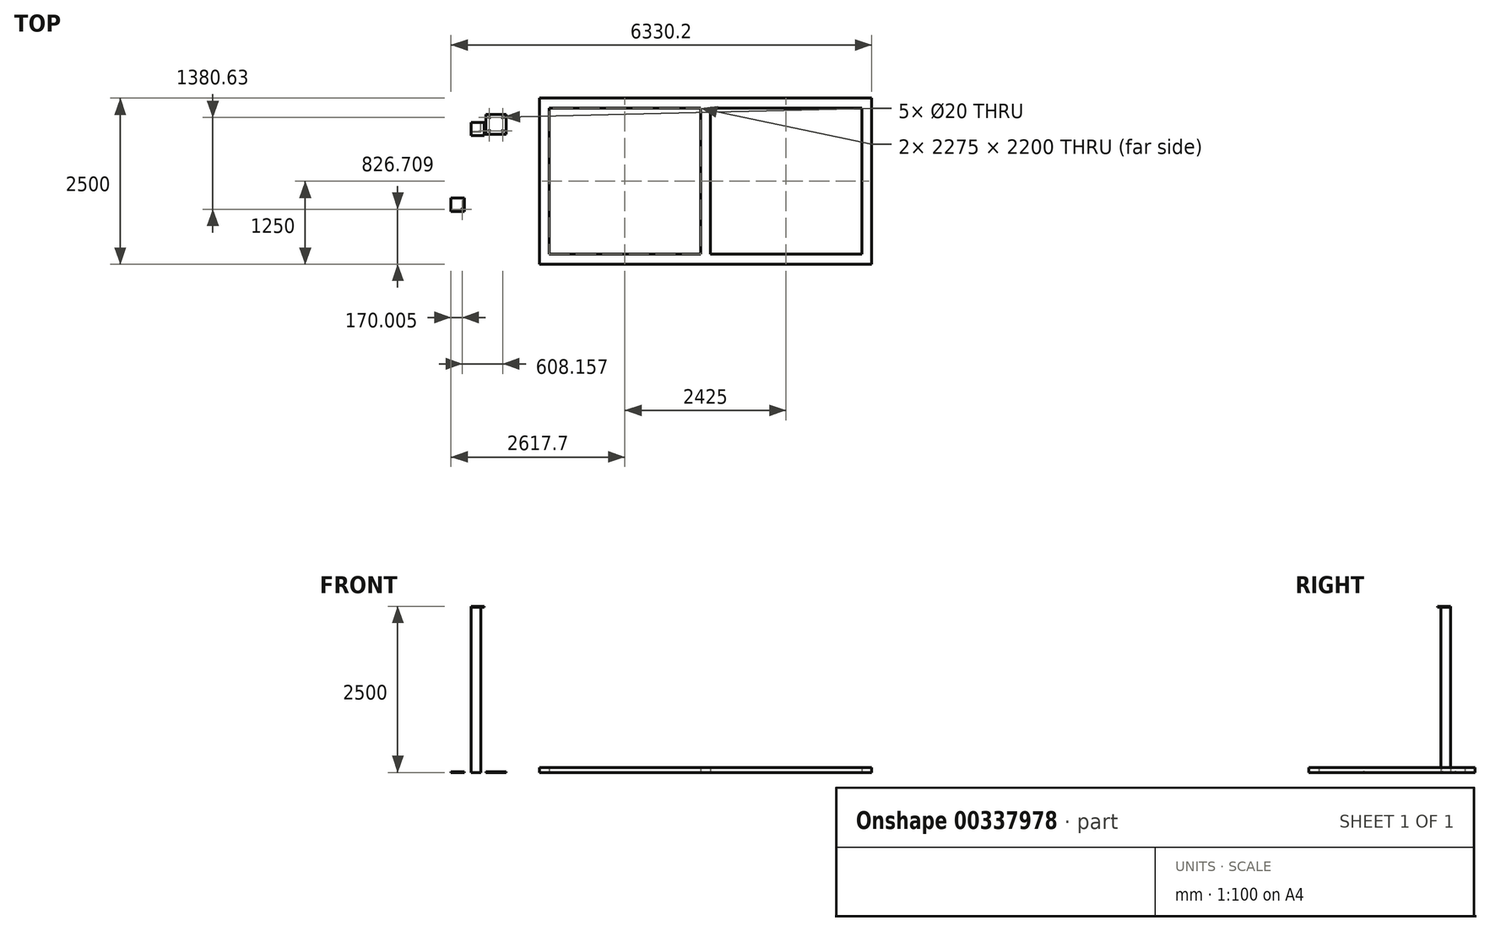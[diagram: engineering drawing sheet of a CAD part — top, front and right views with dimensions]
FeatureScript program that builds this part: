
annotation { "Feature Type Name" : "Feature", "Feature Type Description" : "" }
export const myFeature = defineFeature(function(context is Context, id is Id, definition is map)
    precondition{}
    {
        {
            var Q0;
            Q0=qCreatedBy(makeId("Top.planeOp"),FACE);
            var sketch = newSketch(context, id + "F0", { "sketchPlane" : qUnion([Q0])});
            skLineSegment(sketch, "E0.bottom", {"start": v(75, -75) * mm, "end": v(-75, -75) * mm});
            skLineSegment(sketch, "E0.top", {"start": v(75, 75) * mm, "end": v(-75, 75) * mm});
            skLineSegment(sketch, "E0.left", {"start": v(75, -75) * mm, "end": v(75, 75) * mm});
            skLineSegment(sketch, "E0.right", {"start": v(-75, -75) * mm, "end": v(-75, 75) * mm});
            skPoint(sketch, "E0.middle", {"position": v(0, 0) * mm});
            skLineSegment(sketch, "E1.0", {"start": v(70, 70) * mm, "end": v(-70, 70) * mm});
            skLineSegment(sketch, "E1.1", {"start": v(70, -70) * mm, "end": v(70, 70) * mm});
            skLineSegment(sketch, "E1.2", {"start": v(70, -70) * mm, "end": v(-70, -70) * mm});
            skLineSegment(sketch, "E1.3", {"start": v(-70, -70) * mm, "end": v(-70, 70) * mm});
            skLineSegment(sketch, "E2.bottom", {"start": v(451.01, -103.82) * mm, "end": v(151.01, -103.82) * mm});
            skLineSegment(sketch, "E2.top", {"start": v(451.01, 196.18) * mm, "end": v(151.01, 196.18) * mm});
            skLineSegment(sketch, "E2.left", {"start": v(451.01, -103.82) * mm, "end": v(451.01, 196.18) * mm});
            skLineSegment(sketch, "E2.right", {"start": v(151.01, -103.82) * mm, "end": v(151.01, 196.18) * mm});
            skCircle(sketch, "E3", {"center": v(401.01, 146.18) * mm, "radius": 10 * mm});
            skPoint(sketch, "E4", {"position": v(301.01, 46.18) * mm});
            skCircle(sketch, "E5.1.0", {"center": v(201.01, 146.18) * mm, "radius": 10 * mm});
            skCircle(sketch, "E5.2.0", {"center": v(201.01, -53.82) * mm, "radius": 10 * mm});
            skCircle(sketch, "E5.3.0", {"center": v(401.01, -53.82) * mm, "radius": 10 * mm});
            skLineSegment(sketch, "E6", {"start": v(953.05, 438.84) * mm, "end": v(953.05, -2061.16) * mm});
            skLineSegment(sketch, "E7", {"start": v(953.05, -2061.16) * mm, "end": v(5953.05, -2061.16) * mm});
            skLineSegment(sketch, "E8", {"start": v(5953.05, -2061.16) * mm, "end": v(5953.05, 438.84) * mm});
            skLineSegment(sketch, "E9.0", {"start": v(5803.05, -1911.16) * mm, "end": v(5803.05, 288.84) * mm});
            skLineSegment(sketch, "E9.1", {"start": v(1103.05, -1911.16) * mm, "end": v(3378.05, -1911.16) * mm});
            skLineSegment(sketch, "E9.2", {"start": v(1103.05, 288.84) * mm, "end": v(1103.05, -1911.16) * mm});
            skLineSegment(sketch, "E10.0", {"start": v(3528.05, 288.84) * mm, "end": v(3528.05, -1911.16) * mm});
            skLineSegment(sketch, "E11.0", {"start": v(3378.05, 288.84) * mm, "end": v(3378.05, -1911.16) * mm});
            skLineSegment(sketch, "E12.trimOffspring", {"start": v(3528.05, -1911.16) * mm, "end": v(5803.05, -1911.16) * mm});
            skLineSegment(sketch, "E13", {"start": v(953.05, 438.84) * mm, "end": v(1103.05, 438.84) * mm});
            skLineSegment(sketch, "E14", {"start": v(3378.05, 438.84) * mm, "end": v(3528.05, 438.84) * mm});
            skLineSegment(sketch, "E15", {"start": v(5803.05, 438.84) * mm, "end": v(5953.05, 438.84) * mm});
            skLineSegment(sketch, "E16", {"start": v(953.05, 438.84) * mm, "end": v(5953.05, 438.84) * mm});
            skLineSegment(sketch, "E17.0", {"start": v(1103.05, 288.84) * mm, "end": v(3378.05, 288.84) * mm});
            skLineSegment(sketch, "E18.trimOffspring", {"start": v(3528.05, 288.84) * mm, "end": v(5803.05, 288.84) * mm});
            skLineSegment(sketch, "E19.bottom", {"start": v(-177.15, -1264.45) * mm, "end": v(-377.15, -1264.45) * mm});
            skLineSegment(sketch, "E19.top", {"start": v(-177.15, -1064.45) * mm, "end": v(-377.15, -1064.45) * mm});
            skLineSegment(sketch, "E19.left", {"start": v(-177.15, -1264.45) * mm, "end": v(-177.15, -1064.45) * mm});
            skLineSegment(sketch, "E19.right", {"start": v(-377.15, -1264.45) * mm, "end": v(-377.15, -1064.45) * mm});
            skPoint(sketch, "E19.middle", {"position": v(-277.15, -1164.45) * mm});
            skCircle(sketch, "E20", {"center": v(-207.15, -1234.45) * mm, "radius": 10 * mm});
            skSolve(sketch);
        }
        {
            var Q0;
            Q0=makeQuery(id+"F0.imprint","IMPRINT",FACE,{"disambiguationData":[TD([[makeQuery(id+"F0.imprint","IMPRINT",EDGE,{"derivedFrom":sQuery(id+"F0.wireOp",EDGE,"E0.bottom")}),-1.0]])]});
            extrude(context, id + "F1", {"entities" : qUnion([Q0]), "depth" : 2500 * mm});
        }
        {
            var Q0;
            Q0=makeQuery(id+"F0.imprint","IMPRINT",FACE,{"disambiguationData":[TD([[makeQuery(id+"F0.imprint","IMPRINT",EDGE,{"derivedFrom":sQuery(id+"F0.wireOp",EDGE,"E2.bottom")}),-1.0]])]});
            extrude(context, id + "F2", {"entities" : qUnion([Q0]), "depth" : 10 * mm});
        }
        {
            var Q0;
            Q0=makeQuery(id+"F0.imprint","IMPRINT",FACE,{"disambiguationData":[TD([[makeQuery(id+"F0.imprint","IMPRINT",EDGE,{"derivedFrom":sQuery(id+"F0.wireOp",EDGE,"E6")}),1.0]])]});
            extrude(context, id + "F3", {"entities" : qUnion([Q0]), "depth" : 75 * mm});
        }
        {
            var Q0;
            Q0=makeQuery(id+"F0.imprint","IMPRINT",FACE,{"disambiguationData":[TD([[makeQuery(id+"F0.imprint","IMPRINT",EDGE,{"derivedFrom":sQuery(id+"F0.wireOp",EDGE,"E19.bottom")}),-1.0]])]});
            extrude(context, id + "F4", {"entities" : qUnion([Q0]), "depth" : 10 * mm});
        }
        {
            var Q0;
            Q0=makeQuery(id+"F1.opExtrude","CAP_FACE",FACE,{"disambiguationData":[OSD([sQuery(id+"F0.wireOp",EDGE,"E0.bottom"),sQuery(id+"F0.wireOp",EDGE,"E0.top"),sQuery(id+"F0.wireOp",EDGE,"E0.left"),sQuery(id+"F0.wireOp",EDGE,"E0.right"),sQuery(id+"F0.wireOp",EDGE,"E1.0"),sQuery(id+"F0.wireOp",EDGE,"E1.1"),sQuery(id+"F0.wireOp",EDGE,"E1.2"),sQuery(id+"F0.wireOp",EDGE,"E1.3")])],"isStart":false});
            var sketch = newSketch(context, id + "F5", { "sketchPlane" : qUnion([Q0])});
            skLineSegment(sketch, "E21.bottom", {"start": v(-75, 75) * mm, "end": v(125, 75) * mm});
            skLineSegment(sketch, "E21.top", {"start": v(-75, -125) * mm, "end": v(125, -125) * mm});
            skLineSegment(sketch, "E21.left", {"start": v(-75, 75) * mm, "end": v(-75, -125) * mm});
            skLineSegment(sketch, "E21.right", {"start": v(125, 75) * mm, "end": v(125, -125) * mm});
            skLineSegment(sketch, "E22.bottom", {"start": v(-70.63, 75) * mm, "end": v(-75, 75) * mm});
            skLineSegment(sketch, "E22.top", {"start": v(-70.63, 75) * mm, "end": v(-75, 75) * mm});
            skLineSegment(sketch, "E22.left", {"start": v(-70.63, 75) * mm, "end": v(-70.63, 75) * mm});
            skLineSegment(sketch, "E22.right", {"start": v(-75, 75) * mm, "end": v(-75, 75) * mm});
            skLineSegment(sketch, "E23.bottom", {"start": v(75, -75) * mm, "end": v(-75, -75) * mm});
            skLineSegment(sketch, "E23.top", {"start": v(75, 75) * mm, "end": v(-75, 75) * mm});
            skLineSegment(sketch, "E23.left", {"start": v(75, -75) * mm, "end": v(75, 75) * mm});
            skLineSegment(sketch, "E23.right", {"start": v(-75, -75) * mm, "end": v(-75, 75) * mm});
            skSolve(sketch);
        }
        {
            var Q0;
            Q0=makeQuery(id+"F5.imprint","IMPRINT",FACE,{"disambiguationData":[TD([[makeQuery(id+"F5.imprint","IMPRINT",EDGE,{"derivedFrom":sQuery(id+"F5.wireOp",EDGE,"E21.bottom")}),-1.0]])]});
            var Q1;
            Q1=makeQuery(id+"F5.imprint","IMPRINT",FACE,{"disambiguationData":[TD([[makeQuery(id+"F5.imprint","IMPRINT",EDGE,{"derivedFrom":makeQuery(id+"F1.opExtrude","CAP_EDGE",EDGE,{"disambiguationData":[OSD([sQuery(id+"F0.wireOp",EDGE,"E1.0")])],"isStart":false})}),1.0]])]});
            extrude(context, id + "F6", {"entities" : qUnion([Q0, Q1]), "operationType" : NewBodyOperationType.ADD, "depth" : -10 * mm});
        }
    });
